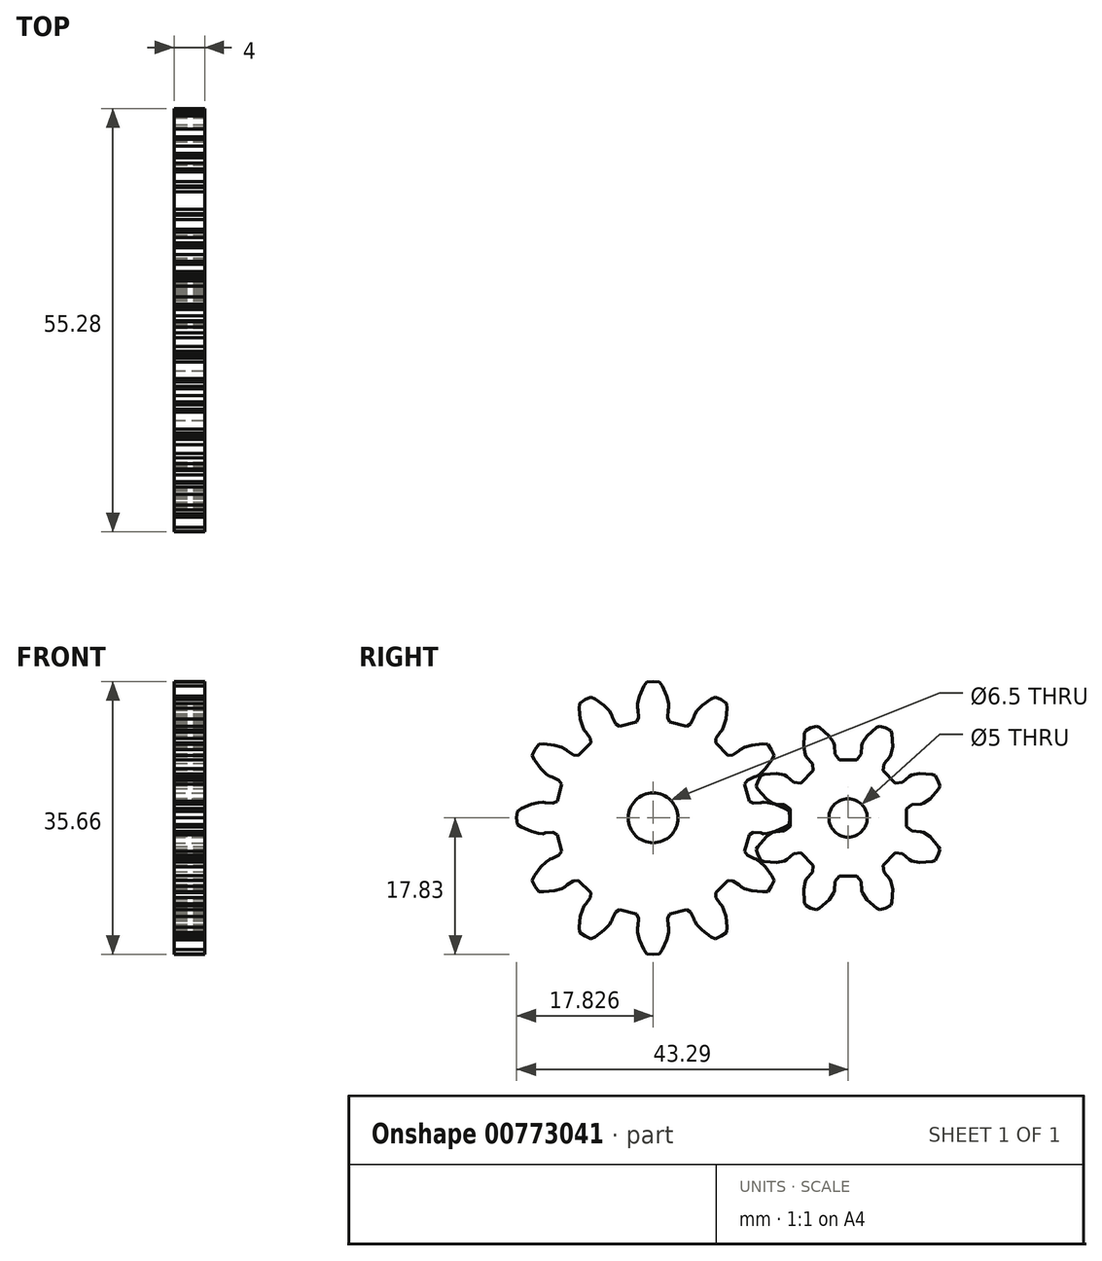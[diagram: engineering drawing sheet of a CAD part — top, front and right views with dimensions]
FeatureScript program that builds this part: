
annotation { "Feature Type Name" : "Feature", "Feature Type Description" : "" }
export const myFeature = defineFeature(function(context is Context, id is Id, definition is map)
    precondition{}
    {
        {
            var Q0;
            Q0=qCreatedBy(makeId("Right.planeOp"),FACE);
            var sketch = newSketch(context, id + "F0", { "sketchPlane" : qUnion([Q0])});
            skLineSegment(sketch, "E0", {"start": v(5.14, -9.6) * mm, "end": v(5.62, -8.91) * mm});
            skLineSegment(sketch, "E1", {"start": v(5.62, -8.91) * mm, "end": v(5.98, -8.15) * mm});
            skLineSegment(sketch, "E2", {"start": v(5.98, -8.15) * mm, "end": v(5.69, -7.55) * mm});
            skLineSegment(sketch, "E3", {"start": v(5.69, -7.55) * mm, "end": v(4.86, -6.4) * mm});
            skLineSegment(sketch, "E4", {"start": v(4.86, -6.4) * mm, "end": v(4.16, -5.74) * mm});
            skLineSegment(sketch, "E5", {"start": v(4.16, -5.74) * mm, "end": v(3.72, -5.44) * mm});
            skLineSegment(sketch, "E6", {"start": v(3.72, -5.44) * mm, "end": v(3.64, -5.4) * mm});
            skLineSegment(sketch, "E7", {"start": v(3.64, -5.4) * mm, "end": v(3.38, -5.34) * mm});
            skLineSegment(sketch, "E8", {"start": v(3.38, -5.34) * mm, "end": v(2.49, -4.9) * mm});
            skLineSegment(sketch, "E9", {"start": v(2.49, -4.9) * mm, "end": v(2.14, -4.38) * mm});
            skLineSegment(sketch, "E10", {"start": v(2.14, -4.38) * mm, "end": v(2.73, -2.18) * mm});
            skLineSegment(sketch, "E11", {"start": v(2.73, -2.18) * mm, "end": v(3.29, -1.91) * mm});
            skLineSegment(sketch, "E12", {"start": v(3.29, -1.91) * mm, "end": v(4.29, -1.97) * mm});
            skLineSegment(sketch, "E13", {"start": v(4.29, -1.97) * mm, "end": v(4.54, -2.04) * mm});
            skLineSegment(sketch, "E14", {"start": v(4.54, -2.04) * mm, "end": v(4.62, -2.05) * mm});
            skLineSegment(sketch, "E15", {"start": v(4.62, -2.05) * mm, "end": v(5.15, -2.02) * mm});
            skLineSegment(sketch, "E16", {"start": v(5.15, -2.02) * mm, "end": v(6.1, -1.79) * mm});
            skLineSegment(sketch, "E17", {"start": v(6.1, -1.79) * mm, "end": v(7.39, -1.21) * mm});
            skLineSegment(sketch, "E18", {"start": v(7.39, -1.21) * mm, "end": v(7.94, -0.84) * mm});
            skLineSegment(sketch, "E19", {"start": v(7.94, -0.84) * mm, "end": v(8.01, 0) * mm});
            skLineSegment(sketch, "E20", {"start": v(8.01, 0) * mm, "end": v(7.94, 0.84) * mm});
            skLineSegment(sketch, "E21", {"start": v(7.94, 0.84) * mm, "end": v(7.39, 1.21) * mm});
            skLineSegment(sketch, "E22", {"start": v(7.39, 1.21) * mm, "end": v(6.1, 1.79) * mm});
            skLineSegment(sketch, "E23", {"start": v(6.1, 1.79) * mm, "end": v(5.15, 2.02) * mm});
            skLineSegment(sketch, "E24", {"start": v(5.15, 2.02) * mm, "end": v(4.62, 2.05) * mm});
            skLineSegment(sketch, "E25", {"start": v(4.62, 2.05) * mm, "end": v(4.54, 2.04) * mm});
            skLineSegment(sketch, "E26", {"start": v(4.54, 2.04) * mm, "end": v(4.29, 1.97) * mm});
            skLineSegment(sketch, "E27", {"start": v(4.29, 1.97) * mm, "end": v(3.29, 1.91) * mm});
            skLineSegment(sketch, "E28", {"start": v(3.29, 1.91) * mm, "end": v(2.73, 2.18) * mm});
            skLineSegment(sketch, "E29", {"start": v(2.73, 2.18) * mm, "end": v(2.14, 4.38) * mm});
            skLineSegment(sketch, "E30", {"start": v(2.14, 4.38) * mm, "end": v(2.49, 4.9) * mm});
            skLineSegment(sketch, "E31", {"start": v(2.49, 4.9) * mm, "end": v(3.38, 5.34) * mm});
            skLineSegment(sketch, "E32", {"start": v(3.38, 5.34) * mm, "end": v(3.64, 5.4) * mm});
            skLineSegment(sketch, "E33", {"start": v(3.64, 5.4) * mm, "end": v(3.72, 5.44) * mm});
            skLineSegment(sketch, "E34", {"start": v(3.72, 5.44) * mm, "end": v(4.16, 5.74) * mm});
            skLineSegment(sketch, "E35", {"start": v(4.16, 5.74) * mm, "end": v(4.86, 6.4) * mm});
            skLineSegment(sketch, "E36", {"start": v(4.86, 6.4) * mm, "end": v(5.69, 7.55) * mm});
            skLineSegment(sketch, "E37", {"start": v(5.69, 7.55) * mm, "end": v(5.98, 8.15) * mm});
            skLineSegment(sketch, "E38", {"start": v(5.98, 8.15) * mm, "end": v(5.62, 8.91) * mm});
            skLineSegment(sketch, "E39", {"start": v(5.62, 8.91) * mm, "end": v(5.14, 9.6) * mm});
            skLineSegment(sketch, "E40", {"start": v(5.14, 9.6) * mm, "end": v(4.48, 9.65) * mm});
            skLineSegment(sketch, "E41", {"start": v(4.48, 9.65) * mm, "end": v(3.07, 9.5) * mm});
            skLineSegment(sketch, "E42", {"start": v(3.07, 9.5) * mm, "end": v(2.14, 9.23) * mm});
            skLineSegment(sketch, "E43", {"start": v(2.14, 9.23) * mm, "end": v(1.66, 9) * mm});
            skLineSegment(sketch, "E44", {"start": v(1.66, 9) * mm, "end": v(1.6, 8.95) * mm});
            skLineSegment(sketch, "E45", {"start": v(1.6, 8.95) * mm, "end": v(1.41, 8.76) * mm});
            skLineSegment(sketch, "E46", {"start": v(1.41, 8.76) * mm, "end": v(0.58, 8.2) * mm});
            skLineSegment(sketch, "E47", {"start": v(0.58, 8.2) * mm, "end": v(-0.04, 8.16) * mm});
            skLineSegment(sketch, "E48", {"start": v(-0.04, 8.16) * mm, "end": v(-1.65, 9.77) * mm});
            skLineSegment(sketch, "E49", {"start": v(-1.65, 9.77) * mm, "end": v(-1.6, 10.4) * mm});
            skLineSegment(sketch, "E50", {"start": v(-1.6, 10.4) * mm, "end": v(-1.06, 11.23) * mm});
            skLineSegment(sketch, "E51", {"start": v(-1.06, 11.23) * mm, "end": v(-0.87, 11.4) * mm});
            skLineSegment(sketch, "E52", {"start": v(-0.87, 11.4) * mm, "end": v(-0.82, 11.48) * mm});
            skLineSegment(sketch, "E53", {"start": v(-0.82, 11.48) * mm, "end": v(-0.58, 11.95) * mm});
            skLineSegment(sketch, "E54", {"start": v(-0.58, 11.95) * mm, "end": v(-0.31, 12.88) * mm});
            skLineSegment(sketch, "E55", {"start": v(-0.31, 12.88) * mm, "end": v(-0.16, 14.29) * mm});
            skLineSegment(sketch, "E56", {"start": v(-0.16, 14.29) * mm, "end": v(-0.2, 14.95) * mm});
            skLineSegment(sketch, "E57", {"start": v(-0.2, 14.95) * mm, "end": v(-0.9, 15.44) * mm});
            skLineSegment(sketch, "E58", {"start": v(-0.9, 15.44) * mm, "end": v(-1.67, 15.8) * mm});
            skLineSegment(sketch, "E59", {"start": v(-1.67, 15.8) * mm, "end": v(-2.26, 15.5) * mm});
            skLineSegment(sketch, "E60", {"start": v(-2.26, 15.5) * mm, "end": v(-3.4, 14.67) * mm});
            skLineSegment(sketch, "E61", {"start": v(-3.4, 14.67) * mm, "end": v(-4.08, 13.97) * mm});
            skLineSegment(sketch, "E62", {"start": v(-4.08, 13.97) * mm, "end": v(-4.37, 13.53) * mm});
            skLineSegment(sketch, "E63", {"start": v(-4.37, 13.53) * mm, "end": v(-4.41, 13.45) * mm});
            skLineSegment(sketch, "E64", {"start": v(-4.41, 13.45) * mm, "end": v(-4.47, 13.2) * mm});
            skLineSegment(sketch, "E65", {"start": v(-4.47, 13.2) * mm, "end": v(-4.92, 12.3) * mm});
            skLineSegment(sketch, "E66", {"start": v(-4.92, 12.3) * mm, "end": v(-5.43, 11.96) * mm});
            skLineSegment(sketch, "E67", {"start": v(-5.43, 11.96) * mm, "end": v(-7.63, 12.54) * mm});
            skLineSegment(sketch, "E68", {"start": v(-7.63, 12.54) * mm, "end": v(-7.9, 13.1) * mm});
            skLineSegment(sketch, "E69", {"start": v(-7.9, 13.1) * mm, "end": v(-7.84, 14.1) * mm});
            skLineSegment(sketch, "E70", {"start": v(-7.84, 14.1) * mm, "end": v(-7.77, 14.35) * mm});
            skLineSegment(sketch, "E71", {"start": v(-7.77, 14.35) * mm, "end": v(-7.76, 14.44) * mm});
            skLineSegment(sketch, "E72", {"start": v(-7.76, 14.44) * mm, "end": v(-7.8, 14.97) * mm});
            skLineSegment(sketch, "E73", {"start": v(-7.8, 14.97) * mm, "end": v(-8.03, 15.9) * mm});
            skLineSegment(sketch, "E74", {"start": v(-8.03, 15.9) * mm, "end": v(-8.6, 17.2) * mm});
            skLineSegment(sketch, "E75", {"start": v(-8.6, 17.2) * mm, "end": v(-8.97, 17.75) * mm});
            skLineSegment(sketch, "E76", {"start": v(-8.97, 17.75) * mm, "end": v(-9.81, 17.83) * mm});
            skLineSegment(sketch, "E77", {"start": v(-9.81, 17.83) * mm, "end": v(-10.66, 17.75) * mm});
            skLineSegment(sketch, "E78", {"start": v(-10.66, 17.75) * mm, "end": v(-11.03, 17.2) * mm});
            skLineSegment(sketch, "E79", {"start": v(-11.03, 17.2) * mm, "end": v(-11.6, 15.9) * mm});
            skLineSegment(sketch, "E80", {"start": v(-11.6, 15.9) * mm, "end": v(-11.83, 14.97) * mm});
            skLineSegment(sketch, "E81", {"start": v(-11.83, 14.97) * mm, "end": v(-11.87, 14.44) * mm});
            skLineSegment(sketch, "E82", {"start": v(-11.87, 14.44) * mm, "end": v(-11.86, 14.35) * mm});
            skLineSegment(sketch, "E83", {"start": v(-11.86, 14.35) * mm, "end": v(-11.79, 14.1) * mm});
            skLineSegment(sketch, "E84", {"start": v(-11.79, 14.1) * mm, "end": v(-11.73, 13.1) * mm});
            skLineSegment(sketch, "E85", {"start": v(-11.73, 13.1) * mm, "end": v(-12, 12.54) * mm});
            skLineSegment(sketch, "E86", {"start": v(-12, 12.54) * mm, "end": v(-14.2, 11.96) * mm});
            skLineSegment(sketch, "E87", {"start": v(-14.2, 11.96) * mm, "end": v(-14.71, 12.3) * mm});
            skLineSegment(sketch, "E88", {"start": v(-14.71, 12.3) * mm, "end": v(-15.16, 13.2) * mm});
            skLineSegment(sketch, "E89", {"start": v(-15.16, 13.2) * mm, "end": v(-15.22, 13.45) * mm});
            skLineSegment(sketch, "E90", {"start": v(-15.22, 13.45) * mm, "end": v(-15.25, 13.53) * mm});
            skLineSegment(sketch, "E91", {"start": v(-15.25, 13.53) * mm, "end": v(-15.55, 13.97) * mm});
            skLineSegment(sketch, "E92", {"start": v(-15.55, 13.97) * mm, "end": v(-16.22, 14.67) * mm});
            skLineSegment(sketch, "E93", {"start": v(-16.22, 14.67) * mm, "end": v(-17.36, 15.5) * mm});
            skLineSegment(sketch, "E94", {"start": v(-17.36, 15.5) * mm, "end": v(-17.96, 15.8) * mm});
            skLineSegment(sketch, "E95", {"start": v(-17.96, 15.8) * mm, "end": v(-18.73, 15.44) * mm});
            skLineSegment(sketch, "E96", {"start": v(-18.73, 15.44) * mm, "end": v(-19.42, 14.95) * mm});
            skLineSegment(sketch, "E97", {"start": v(-19.42, 14.95) * mm, "end": v(-19.47, 14.29) * mm});
            skLineSegment(sketch, "E98", {"start": v(-19.47, 14.29) * mm, "end": v(-19.32, 12.88) * mm});
            skLineSegment(sketch, "E99", {"start": v(-19.32, 12.88) * mm, "end": v(-19.05, 11.95) * mm});
            skLineSegment(sketch, "E100", {"start": v(-19.05, 11.95) * mm, "end": v(-18.81, 11.48) * mm});
            skLineSegment(sketch, "E101", {"start": v(-18.81, 11.48) * mm, "end": v(-18.76, 11.4) * mm});
            skLineSegment(sketch, "E102", {"start": v(-18.76, 11.4) * mm, "end": v(-18.57, 11.23) * mm});
            skLineSegment(sketch, "E103", {"start": v(-18.57, 11.23) * mm, "end": v(-18.02, 10.4) * mm});
            skLineSegment(sketch, "E104", {"start": v(-18.02, 10.4) * mm, "end": v(-17.98, 9.77) * mm});
            skLineSegment(sketch, "E105", {"start": v(-17.98, 9.77) * mm, "end": v(-19.59, 8.16) * mm});
            skLineSegment(sketch, "E106", {"start": v(-19.59, 8.16) * mm, "end": v(-20.2, 8.2) * mm});
            skLineSegment(sketch, "E107", {"start": v(-20.2, 8.2) * mm, "end": v(-21.04, 8.76) * mm});
            skLineSegment(sketch, "E108", {"start": v(-21.04, 8.76) * mm, "end": v(-21.22, 8.95) * mm});
            skLineSegment(sketch, "E109", {"start": v(-21.22, 8.95) * mm, "end": v(-21.3, 9) * mm});
            skLineSegment(sketch, "E110", {"start": v(-21.3, 9) * mm, "end": v(-21.77, 9.23) * mm});
            skLineSegment(sketch, "E111", {"start": v(-21.77, 9.23) * mm, "end": v(-22.7, 9.5) * mm});
            skLineSegment(sketch, "E112", {"start": v(-22.7, 9.5) * mm, "end": v(-24.1, 9.65) * mm});
            skLineSegment(sketch, "E113", {"start": v(-24.1, 9.65) * mm, "end": v(-24.77, 9.6) * mm});
            skLineSegment(sketch, "E114", {"start": v(-24.77, 9.6) * mm, "end": v(-25.25, 8.91) * mm});
            skLineSegment(sketch, "E115", {"start": v(-25.25, 8.91) * mm, "end": v(-25.6, 8.15) * mm});
            skLineSegment(sketch, "E116", {"start": v(-25.6, 8.15) * mm, "end": v(-25.32, 7.55) * mm});
            skLineSegment(sketch, "E117", {"start": v(-25.32, 7.55) * mm, "end": v(-24.48, 6.4) * mm});
            skLineSegment(sketch, "E118", {"start": v(-24.48, 6.4) * mm, "end": v(-23.78, 5.74) * mm});
            skLineSegment(sketch, "E119", {"start": v(-23.78, 5.74) * mm, "end": v(-23.34, 5.44) * mm});
            skLineSegment(sketch, "E120", {"start": v(-23.34, 5.44) * mm, "end": v(-23.26, 5.4) * mm});
            skLineSegment(sketch, "E121", {"start": v(-23.26, 5.4) * mm, "end": v(-23.01, 5.34) * mm});
            skLineSegment(sketch, "E122", {"start": v(-23.01, 5.34) * mm, "end": v(-22.12, 4.9) * mm});
            skLineSegment(sketch, "E123", {"start": v(-22.12, 4.9) * mm, "end": v(-21.77, 4.38) * mm});
            skLineSegment(sketch, "E124", {"start": v(-21.77, 4.38) * mm, "end": v(-22.36, 2.18) * mm});
            skLineSegment(sketch, "E125", {"start": v(-22.36, 2.18) * mm, "end": v(-22.92, 1.91) * mm});
            skLineSegment(sketch, "E126", {"start": v(-22.92, 1.91) * mm, "end": v(-23.92, 1.97) * mm});
            skLineSegment(sketch, "E127", {"start": v(-23.92, 1.97) * mm, "end": v(-24.16, 2.04) * mm});
            skLineSegment(sketch, "E128", {"start": v(-24.16, 2.04) * mm, "end": v(-24.25, 2.05) * mm});
            skLineSegment(sketch, "E129", {"start": v(-24.25, 2.05) * mm, "end": v(-24.78, 2.02) * mm});
            skLineSegment(sketch, "E130", {"start": v(-24.78, 2.02) * mm, "end": v(-25.72, 1.79) * mm});
            skLineSegment(sketch, "E131", {"start": v(-25.72, 1.79) * mm, "end": v(-27.02, 1.21) * mm});
            skLineSegment(sketch, "E132", {"start": v(-27.02, 1.21) * mm, "end": v(-27.57, 0.84) * mm});
            skLineSegment(sketch, "E133", {"start": v(-27.57, 0.84) * mm, "end": v(-27.64, 0) * mm});
            skLineSegment(sketch, "E134", {"start": v(-27.64, 0) * mm, "end": v(-27.57, -0.84) * mm});
            skLineSegment(sketch, "E135", {"start": v(-27.57, -0.84) * mm, "end": v(-27.02, -1.21) * mm});
            skLineSegment(sketch, "E136", {"start": v(-27.02, -1.21) * mm, "end": v(-25.72, -1.79) * mm});
            skLineSegment(sketch, "E137", {"start": v(-25.72, -1.79) * mm, "end": v(-24.78, -2.02) * mm});
            skLineSegment(sketch, "E138", {"start": v(-24.78, -2.02) * mm, "end": v(-24.25, -2.05) * mm});
            skLineSegment(sketch, "E139", {"start": v(-24.25, -2.05) * mm, "end": v(-24.16, -2.04) * mm});
            skLineSegment(sketch, "E140", {"start": v(-24.16, -2.04) * mm, "end": v(-23.92, -1.97) * mm});
            skLineSegment(sketch, "E141", {"start": v(-23.92, -1.97) * mm, "end": v(-22.92, -1.91) * mm});
            skLineSegment(sketch, "E142", {"start": v(-22.92, -1.91) * mm, "end": v(-22.36, -2.18) * mm});
            skLineSegment(sketch, "E143", {"start": v(-22.36, -2.18) * mm, "end": v(-21.77, -4.38) * mm});
            skLineSegment(sketch, "E144", {"start": v(-21.77, -4.38) * mm, "end": v(-22.12, -4.9) * mm});
            skLineSegment(sketch, "E145", {"start": v(-22.12, -4.9) * mm, "end": v(-23.01, -5.34) * mm});
            skLineSegment(sketch, "E146", {"start": v(-23.01, -5.34) * mm, "end": v(-23.26, -5.4) * mm});
            skLineSegment(sketch, "E147", {"start": v(-23.26, -5.4) * mm, "end": v(-23.34, -5.44) * mm});
            skLineSegment(sketch, "E148", {"start": v(-23.34, -5.44) * mm, "end": v(-23.78, -5.74) * mm});
            skLineSegment(sketch, "E149", {"start": v(-23.78, -5.74) * mm, "end": v(-24.48, -6.4) * mm});
            skLineSegment(sketch, "E150", {"start": v(-24.48, -6.4) * mm, "end": v(-25.32, -7.55) * mm});
            skLineSegment(sketch, "E151", {"start": v(-25.32, -7.55) * mm, "end": v(-25.6, -8.15) * mm});
            skLineSegment(sketch, "E152", {"start": v(-25.6, -8.15) * mm, "end": v(-25.25, -8.91) * mm});
            skLineSegment(sketch, "E153", {"start": v(-25.25, -8.91) * mm, "end": v(-24.77, -9.6) * mm});
            skLineSegment(sketch, "E154", {"start": v(-24.77, -9.6) * mm, "end": v(-24.1, -9.65) * mm});
            skLineSegment(sketch, "E155", {"start": v(-24.1, -9.65) * mm, "end": v(-22.7, -9.5) * mm});
            skLineSegment(sketch, "E156", {"start": v(-22.7, -9.5) * mm, "end": v(-21.77, -9.23) * mm});
            skLineSegment(sketch, "E157", {"start": v(-21.77, -9.23) * mm, "end": v(-21.3, -9) * mm});
            skLineSegment(sketch, "E158", {"start": v(-21.3, -9) * mm, "end": v(-21.22, -8.95) * mm});
            skLineSegment(sketch, "E159", {"start": v(-21.22, -8.95) * mm, "end": v(-21.04, -8.76) * mm});
            skLineSegment(sketch, "E160", {"start": v(-21.04, -8.76) * mm, "end": v(-20.2, -8.2) * mm});
            skLineSegment(sketch, "E161", {"start": v(-20.2, -8.2) * mm, "end": v(-19.59, -8.16) * mm});
            skLineSegment(sketch, "E162", {"start": v(-19.59, -8.16) * mm, "end": v(-17.98, -9.77) * mm});
            skLineSegment(sketch, "E163", {"start": v(-17.98, -9.77) * mm, "end": v(-18.02, -10.4) * mm});
            skLineSegment(sketch, "E164", {"start": v(-18.02, -10.4) * mm, "end": v(-18.57, -11.23) * mm});
            skLineSegment(sketch, "E165", {"start": v(-18.57, -11.23) * mm, "end": v(-18.76, -11.4) * mm});
            skLineSegment(sketch, "E166", {"start": v(-18.76, -11.4) * mm, "end": v(-18.81, -11.48) * mm});
            skLineSegment(sketch, "E167", {"start": v(-18.81, -11.48) * mm, "end": v(-19.05, -11.95) * mm});
            skLineSegment(sketch, "E168", {"start": v(-19.05, -11.95) * mm, "end": v(-19.32, -12.88) * mm});
            skLineSegment(sketch, "E169", {"start": v(-19.32, -12.88) * mm, "end": v(-19.47, -14.29) * mm});
            skLineSegment(sketch, "E170", {"start": v(-19.47, -14.29) * mm, "end": v(-19.42, -14.95) * mm});
            skLineSegment(sketch, "E171", {"start": v(-19.42, -14.95) * mm, "end": v(-18.73, -15.44) * mm});
            skLineSegment(sketch, "E172", {"start": v(-18.73, -15.44) * mm, "end": v(-17.96, -15.8) * mm});
            skLineSegment(sketch, "E173", {"start": v(-17.96, -15.8) * mm, "end": v(-17.36, -15.5) * mm});
            skLineSegment(sketch, "E174", {"start": v(-17.36, -15.5) * mm, "end": v(-16.22, -14.67) * mm});
            skLineSegment(sketch, "E175", {"start": v(-16.22, -14.67) * mm, "end": v(-15.55, -13.97) * mm});
            skLineSegment(sketch, "E176", {"start": v(-15.55, -13.97) * mm, "end": v(-15.25, -13.53) * mm});
            skLineSegment(sketch, "E177", {"start": v(-15.25, -13.53) * mm, "end": v(-15.22, -13.45) * mm});
            skLineSegment(sketch, "E178", {"start": v(-15.22, -13.45) * mm, "end": v(-15.16, -13.2) * mm});
            skLineSegment(sketch, "E179", {"start": v(-15.16, -13.2) * mm, "end": v(-14.71, -12.3) * mm});
            skLineSegment(sketch, "E180", {"start": v(-14.71, -12.3) * mm, "end": v(-14.2, -11.96) * mm});
            skLineSegment(sketch, "E181", {"start": v(-14.2, -11.96) * mm, "end": v(-12, -12.54) * mm});
            skLineSegment(sketch, "E182", {"start": v(-12, -12.54) * mm, "end": v(-11.73, -13.1) * mm});
            skLineSegment(sketch, "E183", {"start": v(-11.73, -13.1) * mm, "end": v(-11.79, -14.1) * mm});
            skLineSegment(sketch, "E184", {"start": v(-11.79, -14.1) * mm, "end": v(-11.86, -14.35) * mm});
            skLineSegment(sketch, "E185", {"start": v(-11.86, -14.35) * mm, "end": v(-11.87, -14.44) * mm});
            skLineSegment(sketch, "E186", {"start": v(-11.87, -14.44) * mm, "end": v(-11.83, -14.97) * mm});
            skLineSegment(sketch, "E187", {"start": v(-11.83, -14.97) * mm, "end": v(-11.6, -15.9) * mm});
            skLineSegment(sketch, "E188", {"start": v(-11.6, -15.9) * mm, "end": v(-11.03, -17.2) * mm});
            skLineSegment(sketch, "E189", {"start": v(-11.03, -17.2) * mm, "end": v(-10.66, -17.75) * mm});
            skLineSegment(sketch, "E190", {"start": v(-10.66, -17.75) * mm, "end": v(-9.81, -17.83) * mm});
            skLineSegment(sketch, "E191", {"start": v(-9.81, -17.83) * mm, "end": v(-8.97, -17.75) * mm});
            skLineSegment(sketch, "E192", {"start": v(-8.97, -17.75) * mm, "end": v(-8.6, -17.2) * mm});
            skLineSegment(sketch, "E193", {"start": v(-8.6, -17.2) * mm, "end": v(-8.03, -15.9) * mm});
            skLineSegment(sketch, "E194", {"start": v(-8.03, -15.9) * mm, "end": v(-7.8, -14.97) * mm});
            skLineSegment(sketch, "E195", {"start": v(-7.8, -14.97) * mm, "end": v(-7.76, -14.44) * mm});
            skLineSegment(sketch, "E196", {"start": v(-7.76, -14.44) * mm, "end": v(-7.77, -14.35) * mm});
            skLineSegment(sketch, "E197", {"start": v(-7.77, -14.35) * mm, "end": v(-7.84, -14.1) * mm});
            skLineSegment(sketch, "E198", {"start": v(-7.84, -14.1) * mm, "end": v(-7.9, -13.1) * mm});
            skLineSegment(sketch, "E199", {"start": v(-7.9, -13.1) * mm, "end": v(-7.63, -12.54) * mm});
            skLineSegment(sketch, "E200", {"start": v(-7.63, -12.54) * mm, "end": v(-5.43, -11.96) * mm});
            skLineSegment(sketch, "E201", {"start": v(-5.43, -11.96) * mm, "end": v(-4.92, -12.3) * mm});
            skLineSegment(sketch, "E202", {"start": v(-4.92, -12.3) * mm, "end": v(-4.47, -13.2) * mm});
            skLineSegment(sketch, "E203", {"start": v(-4.47, -13.2) * mm, "end": v(-4.41, -13.45) * mm});
            skLineSegment(sketch, "E204", {"start": v(-4.41, -13.45) * mm, "end": v(-4.37, -13.53) * mm});
            skLineSegment(sketch, "E205", {"start": v(-4.37, -13.53) * mm, "end": v(-4.08, -13.97) * mm});
            skLineSegment(sketch, "E206", {"start": v(-4.08, -13.97) * mm, "end": v(-3.4, -14.67) * mm});
            skLineSegment(sketch, "E207", {"start": v(-3.4, -14.67) * mm, "end": v(-2.26, -15.5) * mm});
            skLineSegment(sketch, "E208", {"start": v(-2.26, -15.5) * mm, "end": v(-1.67, -15.8) * mm});
            skLineSegment(sketch, "E209", {"start": v(-1.67, -15.8) * mm, "end": v(-0.9, -15.44) * mm});
            skLineSegment(sketch, "E210", {"start": v(-0.9, -15.44) * mm, "end": v(-0.2, -14.95) * mm});
            skLineSegment(sketch, "E211", {"start": v(-0.2, -14.95) * mm, "end": v(-0.16, -14.29) * mm});
            skLineSegment(sketch, "E212", {"start": v(-0.16, -14.29) * mm, "end": v(-0.31, -12.88) * mm});
            skLineSegment(sketch, "E213", {"start": v(-0.31, -12.88) * mm, "end": v(-0.58, -11.95) * mm});
            skLineSegment(sketch, "E214", {"start": v(-0.58, -11.95) * mm, "end": v(-0.82, -11.48) * mm});
            skLineSegment(sketch, "E215", {"start": v(-0.82, -11.48) * mm, "end": v(-0.87, -11.4) * mm});
            skLineSegment(sketch, "E216", {"start": v(-0.87, -11.4) * mm, "end": v(-1.06, -11.23) * mm});
            skLineSegment(sketch, "E217", {"start": v(-1.06, -11.23) * mm, "end": v(-1.6, -10.4) * mm});
            skLineSegment(sketch, "E218", {"start": v(-1.6, -10.4) * mm, "end": v(-1.65, -9.77) * mm});
            skLineSegment(sketch, "E219", {"start": v(-1.65, -9.77) * mm, "end": v(-0.04, -8.16) * mm});
            skLineSegment(sketch, "E220", {"start": v(-0.04, -8.16) * mm, "end": v(0.58, -8.2) * mm});
            skLineSegment(sketch, "E221", {"start": v(0.58, -8.2) * mm, "end": v(1.41, -8.76) * mm});
            skLineSegment(sketch, "E222", {"start": v(1.41, -8.76) * mm, "end": v(1.6, -8.95) * mm});
            skLineSegment(sketch, "E223", {"start": v(1.6, -8.95) * mm, "end": v(1.66, -9) * mm});
            skLineSegment(sketch, "E224", {"start": v(1.66, -9) * mm, "end": v(2.14, -9.23) * mm});
            skLineSegment(sketch, "E225", {"start": v(2.14, -9.23) * mm, "end": v(3.07, -9.5) * mm});
            skLineSegment(sketch, "E226", {"start": v(3.07, -9.5) * mm, "end": v(4.48, -9.65) * mm});
            skLineSegment(sketch, "E227", {"start": v(4.48, -9.65) * mm, "end": v(5.14, -9.6) * mm});
            skLineSegment(sketch, "E228", {"start": v(-9.4, -1.96) * mm, "end": v(-9.81, -2) * mm});
            skLineSegment(sketch, "E229", {"start": v(-9.81, -2) * mm, "end": v(-10.23, -1.96) * mm});
            skLineSegment(sketch, "E230", {"start": v(-10.23, -1.96) * mm, "end": v(-10.63, -1.83) * mm});
            skLineSegment(sketch, "E231", {"start": v(-10.63, -1.83) * mm, "end": v(-10.99, -1.62) * mm});
            skLineSegment(sketch, "E232", {"start": v(-10.99, -1.62) * mm, "end": v(-11.3, -1.34) * mm});
            skLineSegment(sketch, "E233", {"start": v(-11.3, -1.34) * mm, "end": v(-11.55, -1) * mm});
            skLineSegment(sketch, "E234", {"start": v(-11.55, -1) * mm, "end": v(-11.72, -0.62) * mm});
            skLineSegment(sketch, "E235", {"start": v(-11.72, -0.62) * mm, "end": v(-11.8, -0.2) * mm});
            skLineSegment(sketch, "E236", {"start": v(-11.8, -0.2) * mm, "end": v(-11.8, 0.2) * mm});
            skLineSegment(sketch, "E237", {"start": v(-11.8, 0.2) * mm, "end": v(-11.72, 0.62) * mm});
            skLineSegment(sketch, "E238", {"start": v(-11.72, 0.62) * mm, "end": v(-11.55, 1) * mm});
            skLineSegment(sketch, "E239", {"start": v(-11.55, 1) * mm, "end": v(-11.3, 1.34) * mm});
            skLineSegment(sketch, "E240", {"start": v(-11.3, 1.34) * mm, "end": v(-10.99, 1.62) * mm});
            skLineSegment(sketch, "E241", {"start": v(-10.99, 1.62) * mm, "end": v(-10.63, 1.83) * mm});
            skLineSegment(sketch, "E242", {"start": v(-10.63, 1.83) * mm, "end": v(-10.23, 1.96) * mm});
            skLineSegment(sketch, "E243", {"start": v(-10.23, 1.96) * mm, "end": v(-9.81, 2) * mm});
            skLineSegment(sketch, "E244", {"start": v(-9.81, 2) * mm, "end": v(-9.4, 1.96) * mm});
            skLineSegment(sketch, "E245", {"start": v(-9.4, 1.96) * mm, "end": v(-9, 1.83) * mm});
            skLineSegment(sketch, "E246", {"start": v(-9, 1.83) * mm, "end": v(-8.64, 1.62) * mm});
            skLineSegment(sketch, "E247", {"start": v(-8.64, 1.62) * mm, "end": v(-8.33, 1.34) * mm});
            skLineSegment(sketch, "E248", {"start": v(-8.33, 1.34) * mm, "end": v(-8.08, 1) * mm});
            skLineSegment(sketch, "E249", {"start": v(-8.08, 1) * mm, "end": v(-7.91, 0.62) * mm});
            skLineSegment(sketch, "E250", {"start": v(-7.91, 0.62) * mm, "end": v(-7.83, 0.2) * mm});
            skLineSegment(sketch, "E251", {"start": v(-7.83, 0.2) * mm, "end": v(-7.83, -0.2) * mm});
            skLineSegment(sketch, "E252", {"start": v(-7.83, -0.2) * mm, "end": v(-7.91, -0.62) * mm});
            skLineSegment(sketch, "E253", {"start": v(-7.91, -0.62) * mm, "end": v(-8.08, -1) * mm});
            skLineSegment(sketch, "E254", {"start": v(-8.08, -1) * mm, "end": v(-8.33, -1.34) * mm});
            skLineSegment(sketch, "E255", {"start": v(-8.33, -1.34) * mm, "end": v(-8.64, -1.62) * mm});
            skLineSegment(sketch, "E256", {"start": v(-8.64, -1.62) * mm, "end": v(-9, -1.83) * mm});
            skLineSegment(sketch, "E257", {"start": v(-9, -1.83) * mm, "end": v(-9.4, -1.96) * mm});
            skLineSegment(sketch, "E258", {"start": v(4.25, 5.56) * mm, "end": v(3.89, 4.87) * mm});
            skLineSegment(sketch, "E259", {"start": v(3.89, 4.87) * mm, "end": v(3.66, 4.13) * mm});
            skLineSegment(sketch, "E260", {"start": v(3.66, 4.13) * mm, "end": v(3.84, 3.76) * mm});
            skLineSegment(sketch, "E261", {"start": v(3.84, 3.76) * mm, "end": v(4.96, 2.48) * mm});
            skLineSegment(sketch, "E262", {"start": v(4.96, 2.48) * mm, "end": v(5.8, 1.9) * mm});
            skLineSegment(sketch, "E263", {"start": v(5.8, 1.9) * mm, "end": v(6.15, 1.8) * mm});
            skLineSegment(sketch, "E264", {"start": v(6.15, 1.8) * mm, "end": v(7.33, 1.71) * mm});
            skLineSegment(sketch, "E265", {"start": v(7.33, 1.71) * mm, "end": v(8.06, 1.14) * mm});
            skLineSegment(sketch, "E266", {"start": v(8.06, 1.14) * mm, "end": v(8.06, -1.14) * mm});
            skLineSegment(sketch, "E267", {"start": v(8.06, -1.14) * mm, "end": v(7.33, -1.71) * mm});
            skLineSegment(sketch, "E268", {"start": v(7.33, -1.71) * mm, "end": v(6.15, -1.8) * mm});
            skLineSegment(sketch, "E269", {"start": v(6.15, -1.8) * mm, "end": v(5.8, -1.9) * mm});
            skLineSegment(sketch, "E270", {"start": v(5.8, -1.9) * mm, "end": v(4.96, -2.48) * mm});
            skLineSegment(sketch, "E271", {"start": v(4.96, -2.48) * mm, "end": v(3.84, -3.76) * mm});
            skLineSegment(sketch, "E272", {"start": v(3.84, -3.76) * mm, "end": v(3.66, -4.13) * mm});
            skLineSegment(sketch, "E273", {"start": v(3.66, -4.13) * mm, "end": v(3.89, -4.87) * mm});
            skLineSegment(sketch, "E274", {"start": v(3.89, -4.87) * mm, "end": v(4.25, -5.56) * mm});
            skLineSegment(sketch, "E275", {"start": v(4.25, -5.56) * mm, "end": v(4.65, -5.7) * mm});
            skLineSegment(sketch, "E276", {"start": v(4.65, -5.7) * mm, "end": v(6.33, -5.8) * mm});
            skLineSegment(sketch, "E277", {"start": v(6.33, -5.8) * mm, "end": v(7.34, -5.6) * mm});
            skLineSegment(sketch, "E278", {"start": v(7.34, -5.6) * mm, "end": v(7.67, -5.45) * mm});
            skLineSegment(sketch, "E279", {"start": v(7.67, -5.45) * mm, "end": v(8.56, -4.67) * mm});
            skLineSegment(sketch, "E280", {"start": v(8.56, -4.67) * mm, "end": v(9.48, -4.56) * mm});
            skLineSegment(sketch, "E281", {"start": v(9.48, -4.56) * mm, "end": v(11.09, -6.17) * mm});
            skLineSegment(sketch, "E282", {"start": v(11.09, -6.17) * mm, "end": v(10.98, -7.1) * mm});
            skLineSegment(sketch, "E283", {"start": v(10.98, -7.1) * mm, "end": v(10.2, -7.98) * mm});
            skLineSegment(sketch, "E284", {"start": v(10.2, -7.98) * mm, "end": v(10.04, -8.3) * mm});
            skLineSegment(sketch, "E285", {"start": v(10.04, -8.3) * mm, "end": v(9.84, -9.32) * mm});
            skLineSegment(sketch, "E286", {"start": v(9.84, -9.32) * mm, "end": v(9.96, -11) * mm});
            skLineSegment(sketch, "E287", {"start": v(9.96, -11) * mm, "end": v(10.1, -11.4) * mm});
            skLineSegment(sketch, "E288", {"start": v(10.1, -11.4) * mm, "end": v(10.78, -11.76) * mm});
            skLineSegment(sketch, "E289", {"start": v(10.78, -11.76) * mm, "end": v(11.52, -11.99) * mm});
            skLineSegment(sketch, "E290", {"start": v(11.52, -11.99) * mm, "end": v(11.9, -11.8) * mm});
            skLineSegment(sketch, "E291", {"start": v(11.9, -11.8) * mm, "end": v(13.17, -10.7) * mm});
            skLineSegment(sketch, "E292", {"start": v(13.17, -10.7) * mm, "end": v(13.74, -9.84) * mm});
            skLineSegment(sketch, "E293", {"start": v(13.74, -9.84) * mm, "end": v(13.86, -9.5) * mm});
            skLineSegment(sketch, "E294", {"start": v(13.86, -9.5) * mm, "end": v(13.94, -8.32) * mm});
            skLineSegment(sketch, "E295", {"start": v(13.94, -8.32) * mm, "end": v(14.51, -7.59) * mm});
            skLineSegment(sketch, "E296", {"start": v(14.51, -7.59) * mm, "end": v(16.79, -7.59) * mm});
            skLineSegment(sketch, "E297", {"start": v(16.79, -7.59) * mm, "end": v(17.36, -8.32) * mm});
            skLineSegment(sketch, "E298", {"start": v(17.36, -8.32) * mm, "end": v(17.44, -9.5) * mm});
            skLineSegment(sketch, "E299", {"start": v(17.44, -9.5) * mm, "end": v(17.56, -9.84) * mm});
            skLineSegment(sketch, "E300", {"start": v(17.56, -9.84) * mm, "end": v(18.13, -10.7) * mm});
            skLineSegment(sketch, "E301", {"start": v(18.13, -10.7) * mm, "end": v(19.4, -11.8) * mm});
            skLineSegment(sketch, "E302", {"start": v(19.4, -11.8) * mm, "end": v(19.78, -11.99) * mm});
            skLineSegment(sketch, "E303", {"start": v(19.78, -11.99) * mm, "end": v(20.52, -11.76) * mm});
            skLineSegment(sketch, "E304", {"start": v(20.52, -11.76) * mm, "end": v(21.2, -11.4) * mm});
            skLineSegment(sketch, "E305", {"start": v(21.2, -11.4) * mm, "end": v(21.34, -11) * mm});
            skLineSegment(sketch, "E306", {"start": v(21.34, -11) * mm, "end": v(21.46, -9.32) * mm});
            skLineSegment(sketch, "E307", {"start": v(21.46, -9.32) * mm, "end": v(21.26, -8.3) * mm});
            skLineSegment(sketch, "E308", {"start": v(21.26, -8.3) * mm, "end": v(21.1, -7.98) * mm});
            skLineSegment(sketch, "E309", {"start": v(21.1, -7.98) * mm, "end": v(20.32, -7.1) * mm});
            skLineSegment(sketch, "E310", {"start": v(20.32, -7.1) * mm, "end": v(20.21, -6.17) * mm});
            skLineSegment(sketch, "E311", {"start": v(20.21, -6.17) * mm, "end": v(21.82, -4.56) * mm});
            skLineSegment(sketch, "E312", {"start": v(21.82, -4.56) * mm, "end": v(22.74, -4.67) * mm});
            skLineSegment(sketch, "E313", {"start": v(22.74, -4.67) * mm, "end": v(23.63, -5.45) * mm});
            skLineSegment(sketch, "E314", {"start": v(23.63, -5.45) * mm, "end": v(23.96, -5.6) * mm});
            skLineSegment(sketch, "E315", {"start": v(23.96, -5.6) * mm, "end": v(24.97, -5.8) * mm});
            skLineSegment(sketch, "E316", {"start": v(24.97, -5.8) * mm, "end": v(26.66, -5.7) * mm});
            skLineSegment(sketch, "E317", {"start": v(26.66, -5.7) * mm, "end": v(27.05, -5.56) * mm});
            skLineSegment(sketch, "E318", {"start": v(27.05, -5.56) * mm, "end": v(27.41, -4.87) * mm});
            skLineSegment(sketch, "E319", {"start": v(27.41, -4.87) * mm, "end": v(27.64, -4.13) * mm});
            skLineSegment(sketch, "E320", {"start": v(27.64, -4.13) * mm, "end": v(27.46, -3.76) * mm});
            skLineSegment(sketch, "E321", {"start": v(27.46, -3.76) * mm, "end": v(26.35, -2.48) * mm});
            skLineSegment(sketch, "E322", {"start": v(26.35, -2.48) * mm, "end": v(25.5, -1.9) * mm});
            skLineSegment(sketch, "E323", {"start": v(25.5, -1.9) * mm, "end": v(25.15, -1.8) * mm});
            skLineSegment(sketch, "E324", {"start": v(25.15, -1.8) * mm, "end": v(23.97, -1.71) * mm});
            skLineSegment(sketch, "E325", {"start": v(23.97, -1.71) * mm, "end": v(23.24, -1.14) * mm});
            skLineSegment(sketch, "E326", {"start": v(23.24, -1.14) * mm, "end": v(23.24, 1.14) * mm});
            skLineSegment(sketch, "E327", {"start": v(23.24, 1.14) * mm, "end": v(23.97, 1.71) * mm});
            skLineSegment(sketch, "E328", {"start": v(23.97, 1.71) * mm, "end": v(25.15, 1.8) * mm});
            skLineSegment(sketch, "E329", {"start": v(25.15, 1.8) * mm, "end": v(25.5, 1.9) * mm});
            skLineSegment(sketch, "E330", {"start": v(25.5, 1.9) * mm, "end": v(26.35, 2.48) * mm});
            skLineSegment(sketch, "E331", {"start": v(26.35, 2.48) * mm, "end": v(27.46, 3.76) * mm});
            skLineSegment(sketch, "E332", {"start": v(27.46, 3.76) * mm, "end": v(27.64, 4.13) * mm});
            skLineSegment(sketch, "E333", {"start": v(27.64, 4.13) * mm, "end": v(27.41, 4.87) * mm});
            skLineSegment(sketch, "E334", {"start": v(27.41, 4.87) * mm, "end": v(27.05, 5.56) * mm});
            skLineSegment(sketch, "E335", {"start": v(27.05, 5.56) * mm, "end": v(26.66, 5.7) * mm});
            skLineSegment(sketch, "E336", {"start": v(26.66, 5.7) * mm, "end": v(24.97, 5.8) * mm});
            skLineSegment(sketch, "E337", {"start": v(24.97, 5.8) * mm, "end": v(23.96, 5.6) * mm});
            skLineSegment(sketch, "E338", {"start": v(23.96, 5.6) * mm, "end": v(23.63, 5.45) * mm});
            skLineSegment(sketch, "E339", {"start": v(23.63, 5.45) * mm, "end": v(22.74, 4.67) * mm});
            skLineSegment(sketch, "E340", {"start": v(22.74, 4.67) * mm, "end": v(21.82, 4.56) * mm});
            skLineSegment(sketch, "E341", {"start": v(21.82, 4.56) * mm, "end": v(20.21, 6.17) * mm});
            skLineSegment(sketch, "E342", {"start": v(20.21, 6.17) * mm, "end": v(20.32, 7.1) * mm});
            skLineSegment(sketch, "E343", {"start": v(20.32, 7.1) * mm, "end": v(21.1, 7.98) * mm});
            skLineSegment(sketch, "E344", {"start": v(21.1, 7.98) * mm, "end": v(21.26, 8.3) * mm});
            skLineSegment(sketch, "E345", {"start": v(21.26, 8.3) * mm, "end": v(21.46, 9.32) * mm});
            skLineSegment(sketch, "E346", {"start": v(21.46, 9.32) * mm, "end": v(21.34, 11) * mm});
            skLineSegment(sketch, "E347", {"start": v(21.34, 11) * mm, "end": v(21.2, 11.4) * mm});
            skLineSegment(sketch, "E348", {"start": v(21.2, 11.4) * mm, "end": v(20.52, 11.76) * mm});
            skLineSegment(sketch, "E349", {"start": v(20.52, 11.76) * mm, "end": v(19.78, 11.99) * mm});
            skLineSegment(sketch, "E350", {"start": v(19.78, 11.99) * mm, "end": v(19.4, 11.8) * mm});
            skLineSegment(sketch, "E351", {"start": v(19.4, 11.8) * mm, "end": v(18.13, 10.7) * mm});
            skLineSegment(sketch, "E352", {"start": v(18.13, 10.7) * mm, "end": v(17.56, 9.84) * mm});
            skLineSegment(sketch, "E353", {"start": v(17.56, 9.84) * mm, "end": v(17.44, 9.5) * mm});
            skLineSegment(sketch, "E354", {"start": v(17.44, 9.5) * mm, "end": v(17.36, 8.32) * mm});
            skLineSegment(sketch, "E355", {"start": v(17.36, 8.32) * mm, "end": v(16.79, 7.59) * mm});
            skLineSegment(sketch, "E356", {"start": v(16.79, 7.59) * mm, "end": v(14.51, 7.59) * mm});
            skLineSegment(sketch, "E357", {"start": v(14.51, 7.59) * mm, "end": v(13.94, 8.32) * mm});
            skLineSegment(sketch, "E358", {"start": v(13.94, 8.32) * mm, "end": v(13.86, 9.5) * mm});
            skLineSegment(sketch, "E359", {"start": v(13.86, 9.5) * mm, "end": v(13.74, 9.84) * mm});
            skLineSegment(sketch, "E360", {"start": v(13.74, 9.84) * mm, "end": v(13.17, 10.7) * mm});
            skLineSegment(sketch, "E361", {"start": v(13.17, 10.7) * mm, "end": v(11.9, 11.8) * mm});
            skLineSegment(sketch, "E362", {"start": v(11.9, 11.8) * mm, "end": v(11.52, 11.99) * mm});
            skLineSegment(sketch, "E363", {"start": v(11.52, 11.99) * mm, "end": v(10.78, 11.76) * mm});
            skLineSegment(sketch, "E364", {"start": v(10.78, 11.76) * mm, "end": v(10.1, 11.4) * mm});
            skLineSegment(sketch, "E365", {"start": v(10.1, 11.4) * mm, "end": v(9.96, 11) * mm});
            skLineSegment(sketch, "E366", {"start": v(9.96, 11) * mm, "end": v(9.84, 9.32) * mm});
            skLineSegment(sketch, "E367", {"start": v(9.84, 9.32) * mm, "end": v(10.04, 8.3) * mm});
            skLineSegment(sketch, "E368", {"start": v(10.04, 8.3) * mm, "end": v(10.2, 7.98) * mm});
            skLineSegment(sketch, "E369", {"start": v(10.2, 7.98) * mm, "end": v(10.98, 7.1) * mm});
            skLineSegment(sketch, "E370", {"start": v(10.98, 7.1) * mm, "end": v(11.09, 6.17) * mm});
            skLineSegment(sketch, "E371", {"start": v(11.09, 6.17) * mm, "end": v(9.48, 4.56) * mm});
            skLineSegment(sketch, "E372", {"start": v(9.48, 4.56) * mm, "end": v(8.56, 4.67) * mm});
            skLineSegment(sketch, "E373", {"start": v(8.56, 4.67) * mm, "end": v(7.67, 5.45) * mm});
            skLineSegment(sketch, "E374", {"start": v(7.67, 5.45) * mm, "end": v(7.34, 5.6) * mm});
            skLineSegment(sketch, "E375", {"start": v(7.34, 5.6) * mm, "end": v(6.33, 5.8) * mm});
            skLineSegment(sketch, "E376", {"start": v(6.33, 5.8) * mm, "end": v(4.65, 5.7) * mm});
            skLineSegment(sketch, "E377", {"start": v(4.65, 5.7) * mm, "end": v(4.25, 5.56) * mm});
            skLineSegment(sketch, "E378", {"start": v(14.52, 1.65) * mm, "end": v(14.89, 1.85) * mm});
            skLineSegment(sketch, "E379", {"start": v(14.89, 1.85) * mm, "end": v(15.29, 1.97) * mm});
            skLineSegment(sketch, "E380", {"start": v(15.29, 1.97) * mm, "end": v(15.7, 2) * mm});
            skLineSegment(sketch, "E381", {"start": v(15.7, 2) * mm, "end": v(16.12, 1.94) * mm});
            skLineSegment(sketch, "E382", {"start": v(16.12, 1.94) * mm, "end": v(16.51, 1.8) * mm});
            skLineSegment(sketch, "E383", {"start": v(16.51, 1.8) * mm, "end": v(16.87, 1.59) * mm});
            skLineSegment(sketch, "E384", {"start": v(16.87, 1.59) * mm, "end": v(17.17, 1.3) * mm});
            skLineSegment(sketch, "E385", {"start": v(17.17, 1.3) * mm, "end": v(17.4, 0.95) * mm});
            skLineSegment(sketch, "E386", {"start": v(17.4, 0.95) * mm, "end": v(17.57, 0.57) * mm});
            skLineSegment(sketch, "E387", {"start": v(17.57, 0.57) * mm, "end": v(17.64, 0.16) * mm});
            skLineSegment(sketch, "E388", {"start": v(17.64, 0.16) * mm, "end": v(17.63, -0.26) * mm});
            skLineSegment(sketch, "E389", {"start": v(17.63, -0.26) * mm, "end": v(17.54, -0.67) * mm});
            skLineSegment(sketch, "E390", {"start": v(17.54, -0.67) * mm, "end": v(17.36, -1.04) * mm});
            skLineSegment(sketch, "E391", {"start": v(17.36, -1.04) * mm, "end": v(17.1, -1.38) * mm});
            skLineSegment(sketch, "E392", {"start": v(17.1, -1.38) * mm, "end": v(16.78, -1.65) * mm});
            skLineSegment(sketch, "E393", {"start": v(16.78, -1.65) * mm, "end": v(16.42, -1.85) * mm});
            skLineSegment(sketch, "E394", {"start": v(16.42, -1.85) * mm, "end": v(16.01, -1.97) * mm});
            skLineSegment(sketch, "E395", {"start": v(16.01, -1.97) * mm, "end": v(15.6, -2) * mm});
            skLineSegment(sketch, "E396", {"start": v(15.6, -2) * mm, "end": v(15.18, -1.94) * mm});
            skLineSegment(sketch, "E397", {"start": v(15.18, -1.94) * mm, "end": v(14.79, -1.8) * mm});
            skLineSegment(sketch, "E398", {"start": v(14.79, -1.8) * mm, "end": v(14.43, -1.59) * mm});
            skLineSegment(sketch, "E399", {"start": v(14.43, -1.59) * mm, "end": v(14.13, -1.3) * mm});
            skLineSegment(sketch, "E400", {"start": v(14.13, -1.3) * mm, "end": v(13.9, -0.95) * mm});
            skLineSegment(sketch, "E401", {"start": v(13.9, -0.95) * mm, "end": v(13.73, -0.57) * mm});
            skLineSegment(sketch, "E402", {"start": v(13.73, -0.57) * mm, "end": v(13.66, -0.16) * mm});
            skLineSegment(sketch, "E403", {"start": v(13.66, -0.16) * mm, "end": v(13.67, 0.26) * mm});
            skLineSegment(sketch, "E404", {"start": v(13.67, 0.26) * mm, "end": v(13.77, 0.67) * mm});
            skLineSegment(sketch, "E405", {"start": v(13.77, 0.67) * mm, "end": v(13.95, 1.04) * mm});
            skLineSegment(sketch, "E406", {"start": v(13.95, 1.04) * mm, "end": v(14.2, 1.38) * mm});
            skLineSegment(sketch, "E407", {"start": v(14.2, 1.38) * mm, "end": v(14.52, 1.65) * mm});
            skSolve(sketch);
        }
        {
            var Q0;
            Q0 = qSketchRegion(id + "F0", true);
            extrude(context, id + "F1", {"entities" : qUnion([Q0]), "depth" : 4 * mm, "offsetDistance" : 25 * mm});
        }
        {
            var Q0;
            Q0=makeQuery(id+"F1.opExtrude","CAP_FACE",FACE,{"disambiguationData":[OSD([sQuery(id+"F0.wireOp",EDGE,"E258"),sQuery(id+"F0.wireOp",EDGE,"E259"),sQuery(id+"F0.wireOp",EDGE,"E260"),sQuery(id+"F0.wireOp",EDGE,"E261"),sQuery(id+"F0.wireOp",EDGE,"E262"),sQuery(id+"F0.wireOp",EDGE,"E263"),sQuery(id+"F0.wireOp",EDGE,"E264"),sQuery(id+"F0.wireOp",EDGE,"E265"),sQuery(id+"F0.wireOp",EDGE,"E266"),sQuery(id+"F0.wireOp",EDGE,"E267"),sQuery(id+"F0.wireOp",EDGE,"E268"),sQuery(id+"F0.wireOp",EDGE,"E269"),sQuery(id+"F0.wireOp",EDGE,"E270"),sQuery(id+"F0.wireOp",EDGE,"E271"),sQuery(id+"F0.wireOp",EDGE,"E272"),sQuery(id+"F0.wireOp",EDGE,"E273"),sQuery(id+"F0.wireOp",EDGE,"E274"),sQuery(id+"F0.wireOp",EDGE,"E275"),sQuery(id+"F0.wireOp",EDGE,"E276"),sQuery(id+"F0.wireOp",EDGE,"E277"),sQuery(id+"F0.wireOp",EDGE,"E278"),sQuery(id+"F0.wireOp",EDGE,"E279"),sQuery(id+"F0.wireOp",EDGE,"E280"),sQuery(id+"F0.wireOp",EDGE,"E281"),sQuery(id+"F0.wireOp",EDGE,"E282"),sQuery(id+"F0.wireOp",EDGE,"E283"),sQuery(id+"F0.wireOp",EDGE,"E284"),sQuery(id+"F0.wireOp",EDGE,"E285"),sQuery(id+"F0.wireOp",EDGE,"E286"),sQuery(id+"F0.wireOp",EDGE,"E287"),sQuery(id+"F0.wireOp",EDGE,"E288"),sQuery(id+"F0.wireOp",EDGE,"E289"),sQuery(id+"F0.wireOp",EDGE,"E290"),sQuery(id+"F0.wireOp",EDGE,"E291"),sQuery(id+"F0.wireOp",EDGE,"E292"),sQuery(id+"F0.wireOp",EDGE,"E293"),sQuery(id+"F0.wireOp",EDGE,"E294"),sQuery(id+"F0.wireOp",EDGE,"E295"),sQuery(id+"F0.wireOp",EDGE,"E296"),sQuery(id+"F0.wireOp",EDGE,"E297"),sQuery(id+"F0.wireOp",EDGE,"E298"),sQuery(id+"F0.wireOp",EDGE,"E299"),sQuery(id+"F0.wireOp",EDGE,"E300"),sQuery(id+"F0.wireOp",EDGE,"E301"),sQuery(id+"F0.wireOp",EDGE,"E302"),sQuery(id+"F0.wireOp",EDGE,"E303"),sQuery(id+"F0.wireOp",EDGE,"E304"),sQuery(id+"F0.wireOp",EDGE,"E305"),sQuery(id+"F0.wireOp",EDGE,"E306"),sQuery(id+"F0.wireOp",EDGE,"E307"),sQuery(id+"F0.wireOp",EDGE,"E308"),sQuery(id+"F0.wireOp",EDGE,"E309"),sQuery(id+"F0.wireOp",EDGE,"E310"),sQuery(id+"F0.wireOp",EDGE,"E311"),sQuery(id+"F0.wireOp",EDGE,"E312"),sQuery(id+"F0.wireOp",EDGE,"E313"),sQuery(id+"F0.wireOp",EDGE,"E314"),sQuery(id+"F0.wireOp",EDGE,"E315"),sQuery(id+"F0.wireOp",EDGE,"E316"),sQuery(id+"F0.wireOp",EDGE,"E317"),sQuery(id+"F0.wireOp",EDGE,"E318"),sQuery(id+"F0.wireOp",EDGE,"E319"),sQuery(id+"F0.wireOp",EDGE,"E320"),sQuery(id+"F0.wireOp",EDGE,"E321"),sQuery(id+"F0.wireOp",EDGE,"E322"),sQuery(id+"F0.wireOp",EDGE,"E323"),sQuery(id+"F0.wireOp",EDGE,"E324"),sQuery(id+"F0.wireOp",EDGE,"E325"),sQuery(id+"F0.wireOp",EDGE,"E326"),sQuery(id+"F0.wireOp",EDGE,"E327"),sQuery(id+"F0.wireOp",EDGE,"E328"),sQuery(id+"F0.wireOp",EDGE,"E329"),sQuery(id+"F0.wireOp",EDGE,"E330"),sQuery(id+"F0.wireOp",EDGE,"E331"),sQuery(id+"F0.wireOp",EDGE,"E332"),sQuery(id+"F0.wireOp",EDGE,"E333"),sQuery(id+"F0.wireOp",EDGE,"E334"),sQuery(id+"F0.wireOp",EDGE,"E335"),sQuery(id+"F0.wireOp",EDGE,"E336"),sQuery(id+"F0.wireOp",EDGE,"E337"),sQuery(id+"F0.wireOp",EDGE,"E338"),sQuery(id+"F0.wireOp",EDGE,"E339"),sQuery(id+"F0.wireOp",EDGE,"E340"),sQuery(id+"F0.wireOp",EDGE,"E341"),sQuery(id+"F0.wireOp",EDGE,"E342"),sQuery(id+"F0.wireOp",EDGE,"E343"),sQuery(id+"F0.wireOp",EDGE,"E344"),sQuery(id+"F0.wireOp",EDGE,"E345"),sQuery(id+"F0.wireOp",EDGE,"E346"),sQuery(id+"F0.wireOp",EDGE,"E347"),sQuery(id+"F0.wireOp",EDGE,"E348"),sQuery(id+"F0.wireOp",EDGE,"E349"),sQuery(id+"F0.wireOp",EDGE,"E350"),sQuery(id+"F0.wireOp",EDGE,"E351"),sQuery(id+"F0.wireOp",EDGE,"E352"),sQuery(id+"F0.wireOp",EDGE,"E353"),sQuery(id+"F0.wireOp",EDGE,"E354"),sQuery(id+"F0.wireOp",EDGE,"E355"),sQuery(id+"F0.wireOp",EDGE,"E356"),sQuery(id+"F0.wireOp",EDGE,"E357"),sQuery(id+"F0.wireOp",EDGE,"E358"),sQuery(id+"F0.wireOp",EDGE,"E359"),sQuery(id+"F0.wireOp",EDGE,"E360"),sQuery(id+"F0.wireOp",EDGE,"E361"),sQuery(id+"F0.wireOp",EDGE,"E362"),sQuery(id+"F0.wireOp",EDGE,"E363"),sQuery(id+"F0.wireOp",EDGE,"E364"),sQuery(id+"F0.wireOp",EDGE,"E365"),sQuery(id+"F0.wireOp",EDGE,"E366"),sQuery(id+"F0.wireOp",EDGE,"E367"),sQuery(id+"F0.wireOp",EDGE,"E368"),sQuery(id+"F0.wireOp",EDGE,"E369"),sQuery(id+"F0.wireOp",EDGE,"E370"),sQuery(id+"F0.wireOp",EDGE,"E371"),sQuery(id+"F0.wireOp",EDGE,"E372"),sQuery(id+"F0.wireOp",EDGE,"E373"),sQuery(id+"F0.wireOp",EDGE,"E374"),sQuery(id+"F0.wireOp",EDGE,"E375"),sQuery(id+"F0.wireOp",EDGE,"E376"),sQuery(id+"F0.wireOp",EDGE,"E377"),sQuery(id+"F0.wireOp",EDGE,"E378"),sQuery(id+"F0.wireOp",EDGE,"E379"),sQuery(id+"F0.wireOp",EDGE,"E380"),sQuery(id+"F0.wireOp",EDGE,"E381"),sQuery(id+"F0.wireOp",EDGE,"E382"),sQuery(id+"F0.wireOp",EDGE,"E383"),sQuery(id+"F0.wireOp",EDGE,"E384"),sQuery(id+"F0.wireOp",EDGE,"E385"),sQuery(id+"F0.wireOp",EDGE,"E386"),sQuery(id+"F0.wireOp",EDGE,"E387"),sQuery(id+"F0.wireOp",EDGE,"E388"),sQuery(id+"F0.wireOp",EDGE,"E389"),sQuery(id+"F0.wireOp",EDGE,"E390"),sQuery(id+"F0.wireOp",EDGE,"E391"),sQuery(id+"F0.wireOp",EDGE,"E392"),sQuery(id+"F0.wireOp",EDGE,"E393"),sQuery(id+"F0.wireOp",EDGE,"E394"),sQuery(id+"F0.wireOp",EDGE,"E395"),sQuery(id+"F0.wireOp",EDGE,"E396"),sQuery(id+"F0.wireOp",EDGE,"E397"),sQuery(id+"F0.wireOp",EDGE,"E398"),sQuery(id+"F0.wireOp",EDGE,"E399"),sQuery(id+"F0.wireOp",EDGE,"E400"),sQuery(id+"F0.wireOp",EDGE,"E401"),sQuery(id+"F0.wireOp",EDGE,"E402"),sQuery(id+"F0.wireOp",EDGE,"E403"),sQuery(id+"F0.wireOp",EDGE,"E404"),sQuery(id+"F0.wireOp",EDGE,"E405"),sQuery(id+"F0.wireOp",EDGE,"E406"),sQuery(id+"F0.wireOp",EDGE,"E407")])],"isStart":false});
            var sketch = newSketch(context, id + "F2", { "sketchPlane" : qUnion([Q0])});
            skCircle(sketch, "E408", {"center": v(15.65, 0) * mm, "radius": 2.5 * mm});
            skLineSegment(sketch, "E409", {"start": v(14.01, -1.13) * mm, "end": v(16.12, 0.32) * mm, "construction": true});
            skLineSegment(sketch, "E410", {"start": v(15.09, 1.9) * mm, "end": v(15.86, -0.71) * mm, "construction": true});
            skSolve(sketch);
        }
        {
            var Q0;
            Q0 = qSketchRegion(id + "F2", true);
            extrude(context, id + "F3", {"entities" : qUnion([Q0]), "operationType" : NewBodyOperationType.REMOVE, "oppositeDirection" : true, "depth" : 25 * mm, "offsetDistance" : 25 * mm});
        }
        {
            var Q0;
            Q0=makeQuery(id+"F1.opExtrude","CAP_FACE",FACE,{"disambiguationData":[OSD([sQuery(id+"F0.wireOp",EDGE,"E0"),sQuery(id+"F0.wireOp",EDGE,"E1"),sQuery(id+"F0.wireOp",EDGE,"E2"),sQuery(id+"F0.wireOp",EDGE,"E3"),sQuery(id+"F0.wireOp",EDGE,"E4"),sQuery(id+"F0.wireOp",EDGE,"E5"),sQuery(id+"F0.wireOp",EDGE,"E6"),sQuery(id+"F0.wireOp",EDGE,"E7"),sQuery(id+"F0.wireOp",EDGE,"E8"),sQuery(id+"F0.wireOp",EDGE,"E9"),sQuery(id+"F0.wireOp",EDGE,"E10"),sQuery(id+"F0.wireOp",EDGE,"E11"),sQuery(id+"F0.wireOp",EDGE,"E12"),sQuery(id+"F0.wireOp",EDGE,"E13"),sQuery(id+"F0.wireOp",EDGE,"E14"),sQuery(id+"F0.wireOp",EDGE,"E15"),sQuery(id+"F0.wireOp",EDGE,"E16"),sQuery(id+"F0.wireOp",EDGE,"E17"),sQuery(id+"F0.wireOp",EDGE,"E18"),sQuery(id+"F0.wireOp",EDGE,"E19"),sQuery(id+"F0.wireOp",EDGE,"E20"),sQuery(id+"F0.wireOp",EDGE,"E21"),sQuery(id+"F0.wireOp",EDGE,"E22"),sQuery(id+"F0.wireOp",EDGE,"E23"),sQuery(id+"F0.wireOp",EDGE,"E24"),sQuery(id+"F0.wireOp",EDGE,"E25"),sQuery(id+"F0.wireOp",EDGE,"E26"),sQuery(id+"F0.wireOp",EDGE,"E27"),sQuery(id+"F0.wireOp",EDGE,"E28"),sQuery(id+"F0.wireOp",EDGE,"E29"),sQuery(id+"F0.wireOp",EDGE,"E30"),sQuery(id+"F0.wireOp",EDGE,"E31"),sQuery(id+"F0.wireOp",EDGE,"E32"),sQuery(id+"F0.wireOp",EDGE,"E33"),sQuery(id+"F0.wireOp",EDGE,"E34"),sQuery(id+"F0.wireOp",EDGE,"E35"),sQuery(id+"F0.wireOp",EDGE,"E36"),sQuery(id+"F0.wireOp",EDGE,"E37"),sQuery(id+"F0.wireOp",EDGE,"E38"),sQuery(id+"F0.wireOp",EDGE,"E39"),sQuery(id+"F0.wireOp",EDGE,"E40"),sQuery(id+"F0.wireOp",EDGE,"E41"),sQuery(id+"F0.wireOp",EDGE,"E42"),sQuery(id+"F0.wireOp",EDGE,"E43"),sQuery(id+"F0.wireOp",EDGE,"E44"),sQuery(id+"F0.wireOp",EDGE,"E45"),sQuery(id+"F0.wireOp",EDGE,"E46"),sQuery(id+"F0.wireOp",EDGE,"E47"),sQuery(id+"F0.wireOp",EDGE,"E48"),sQuery(id+"F0.wireOp",EDGE,"E49"),sQuery(id+"F0.wireOp",EDGE,"E50"),sQuery(id+"F0.wireOp",EDGE,"E51"),sQuery(id+"F0.wireOp",EDGE,"E52"),sQuery(id+"F0.wireOp",EDGE,"E53"),sQuery(id+"F0.wireOp",EDGE,"E54"),sQuery(id+"F0.wireOp",EDGE,"E55"),sQuery(id+"F0.wireOp",EDGE,"E56"),sQuery(id+"F0.wireOp",EDGE,"E57"),sQuery(id+"F0.wireOp",EDGE,"E58"),sQuery(id+"F0.wireOp",EDGE,"E59"),sQuery(id+"F0.wireOp",EDGE,"E60"),sQuery(id+"F0.wireOp",EDGE,"E61"),sQuery(id+"F0.wireOp",EDGE,"E62"),sQuery(id+"F0.wireOp",EDGE,"E63"),sQuery(id+"F0.wireOp",EDGE,"E64"),sQuery(id+"F0.wireOp",EDGE,"E65"),sQuery(id+"F0.wireOp",EDGE,"E66"),sQuery(id+"F0.wireOp",EDGE,"E67"),sQuery(id+"F0.wireOp",EDGE,"E68"),sQuery(id+"F0.wireOp",EDGE,"E69"),sQuery(id+"F0.wireOp",EDGE,"E70"),sQuery(id+"F0.wireOp",EDGE,"E71"),sQuery(id+"F0.wireOp",EDGE,"E72"),sQuery(id+"F0.wireOp",EDGE,"E73"),sQuery(id+"F0.wireOp",EDGE,"E74"),sQuery(id+"F0.wireOp",EDGE,"E75"),sQuery(id+"F0.wireOp",EDGE,"E76"),sQuery(id+"F0.wireOp",EDGE,"E77"),sQuery(id+"F0.wireOp",EDGE,"E78"),sQuery(id+"F0.wireOp",EDGE,"E79"),sQuery(id+"F0.wireOp",EDGE,"E80"),sQuery(id+"F0.wireOp",EDGE,"E81"),sQuery(id+"F0.wireOp",EDGE,"E82"),sQuery(id+"F0.wireOp",EDGE,"E83"),sQuery(id+"F0.wireOp",EDGE,"E84"),sQuery(id+"F0.wireOp",EDGE,"E85"),sQuery(id+"F0.wireOp",EDGE,"E86"),sQuery(id+"F0.wireOp",EDGE,"E87"),sQuery(id+"F0.wireOp",EDGE,"E88"),sQuery(id+"F0.wireOp",EDGE,"E89"),sQuery(id+"F0.wireOp",EDGE,"E90"),sQuery(id+"F0.wireOp",EDGE,"E91"),sQuery(id+"F0.wireOp",EDGE,"E92"),sQuery(id+"F0.wireOp",EDGE,"E93"),sQuery(id+"F0.wireOp",EDGE,"E94"),sQuery(id+"F0.wireOp",EDGE,"E95"),sQuery(id+"F0.wireOp",EDGE,"E96"),sQuery(id+"F0.wireOp",EDGE,"E97"),sQuery(id+"F0.wireOp",EDGE,"E98"),sQuery(id+"F0.wireOp",EDGE,"E99"),sQuery(id+"F0.wireOp",EDGE,"E100"),sQuery(id+"F0.wireOp",EDGE,"E101"),sQuery(id+"F0.wireOp",EDGE,"E102"),sQuery(id+"F0.wireOp",EDGE,"E103"),sQuery(id+"F0.wireOp",EDGE,"E104"),sQuery(id+"F0.wireOp",EDGE,"E105"),sQuery(id+"F0.wireOp",EDGE,"E106"),sQuery(id+"F0.wireOp",EDGE,"E107"),sQuery(id+"F0.wireOp",EDGE,"E108"),sQuery(id+"F0.wireOp",EDGE,"E109"),sQuery(id+"F0.wireOp",EDGE,"E110"),sQuery(id+"F0.wireOp",EDGE,"E111"),sQuery(id+"F0.wireOp",EDGE,"E112"),sQuery(id+"F0.wireOp",EDGE,"E113"),sQuery(id+"F0.wireOp",EDGE,"E114"),sQuery(id+"F0.wireOp",EDGE,"E115"),sQuery(id+"F0.wireOp",EDGE,"E116"),sQuery(id+"F0.wireOp",EDGE,"E117"),sQuery(id+"F0.wireOp",EDGE,"E118"),sQuery(id+"F0.wireOp",EDGE,"E119"),sQuery(id+"F0.wireOp",EDGE,"E120"),sQuery(id+"F0.wireOp",EDGE,"E121"),sQuery(id+"F0.wireOp",EDGE,"E122"),sQuery(id+"F0.wireOp",EDGE,"E123"),sQuery(id+"F0.wireOp",EDGE,"E124"),sQuery(id+"F0.wireOp",EDGE,"E125"),sQuery(id+"F0.wireOp",EDGE,"E126"),sQuery(id+"F0.wireOp",EDGE,"E127"),sQuery(id+"F0.wireOp",EDGE,"E128"),sQuery(id+"F0.wireOp",EDGE,"E129"),sQuery(id+"F0.wireOp",EDGE,"E130"),sQuery(id+"F0.wireOp",EDGE,"E131"),sQuery(id+"F0.wireOp",EDGE,"E132"),sQuery(id+"F0.wireOp",EDGE,"E133"),sQuery(id+"F0.wireOp",EDGE,"E134"),sQuery(id+"F0.wireOp",EDGE,"E135"),sQuery(id+"F0.wireOp",EDGE,"E136"),sQuery(id+"F0.wireOp",EDGE,"E137"),sQuery(id+"F0.wireOp",EDGE,"E138"),sQuery(id+"F0.wireOp",EDGE,"E139"),sQuery(id+"F0.wireOp",EDGE,"E140"),sQuery(id+"F0.wireOp",EDGE,"E141"),sQuery(id+"F0.wireOp",EDGE,"E142"),sQuery(id+"F0.wireOp",EDGE,"E143"),sQuery(id+"F0.wireOp",EDGE,"E144"),sQuery(id+"F0.wireOp",EDGE,"E145"),sQuery(id+"F0.wireOp",EDGE,"E146"),sQuery(id+"F0.wireOp",EDGE,"E147"),sQuery(id+"F0.wireOp",EDGE,"E148"),sQuery(id+"F0.wireOp",EDGE,"E149"),sQuery(id+"F0.wireOp",EDGE,"E150"),sQuery(id+"F0.wireOp",EDGE,"E151"),sQuery(id+"F0.wireOp",EDGE,"E152"),sQuery(id+"F0.wireOp",EDGE,"E153"),sQuery(id+"F0.wireOp",EDGE,"E154"),sQuery(id+"F0.wireOp",EDGE,"E155"),sQuery(id+"F0.wireOp",EDGE,"E156"),sQuery(id+"F0.wireOp",EDGE,"E157"),sQuery(id+"F0.wireOp",EDGE,"E158"),sQuery(id+"F0.wireOp",EDGE,"E159"),sQuery(id+"F0.wireOp",EDGE,"E160"),sQuery(id+"F0.wireOp",EDGE,"E161"),sQuery(id+"F0.wireOp",EDGE,"E162"),sQuery(id+"F0.wireOp",EDGE,"E163"),sQuery(id+"F0.wireOp",EDGE,"E164"),sQuery(id+"F0.wireOp",EDGE,"E165"),sQuery(id+"F0.wireOp",EDGE,"E166"),sQuery(id+"F0.wireOp",EDGE,"E167"),sQuery(id+"F0.wireOp",EDGE,"E168"),sQuery(id+"F0.wireOp",EDGE,"E169"),sQuery(id+"F0.wireOp",EDGE,"E170"),sQuery(id+"F0.wireOp",EDGE,"E171"),sQuery(id+"F0.wireOp",EDGE,"E172"),sQuery(id+"F0.wireOp",EDGE,"E173"),sQuery(id+"F0.wireOp",EDGE,"E174"),sQuery(id+"F0.wireOp",EDGE,"E175"),sQuery(id+"F0.wireOp",EDGE,"E176"),sQuery(id+"F0.wireOp",EDGE,"E177"),sQuery(id+"F0.wireOp",EDGE,"E178"),sQuery(id+"F0.wireOp",EDGE,"E179"),sQuery(id+"F0.wireOp",EDGE,"E180"),sQuery(id+"F0.wireOp",EDGE,"E181"),sQuery(id+"F0.wireOp",EDGE,"E182"),sQuery(id+"F0.wireOp",EDGE,"E183"),sQuery(id+"F0.wireOp",EDGE,"E184"),sQuery(id+"F0.wireOp",EDGE,"E185"),sQuery(id+"F0.wireOp",EDGE,"E186"),sQuery(id+"F0.wireOp",EDGE,"E187"),sQuery(id+"F0.wireOp",EDGE,"E188"),sQuery(id+"F0.wireOp",EDGE,"E189"),sQuery(id+"F0.wireOp",EDGE,"E190"),sQuery(id+"F0.wireOp",EDGE,"E191"),sQuery(id+"F0.wireOp",EDGE,"E192"),sQuery(id+"F0.wireOp",EDGE,"E193"),sQuery(id+"F0.wireOp",EDGE,"E194"),sQuery(id+"F0.wireOp",EDGE,"E195"),sQuery(id+"F0.wireOp",EDGE,"E196"),sQuery(id+"F0.wireOp",EDGE,"E197"),sQuery(id+"F0.wireOp",EDGE,"E198"),sQuery(id+"F0.wireOp",EDGE,"E199"),sQuery(id+"F0.wireOp",EDGE,"E200"),sQuery(id+"F0.wireOp",EDGE,"E201"),sQuery(id+"F0.wireOp",EDGE,"E202"),sQuery(id+"F0.wireOp",EDGE,"E203"),sQuery(id+"F0.wireOp",EDGE,"E204"),sQuery(id+"F0.wireOp",EDGE,"E205"),sQuery(id+"F0.wireOp",EDGE,"E206"),sQuery(id+"F0.wireOp",EDGE,"E207"),sQuery(id+"F0.wireOp",EDGE,"E208"),sQuery(id+"F0.wireOp",EDGE,"E209"),sQuery(id+"F0.wireOp",EDGE,"E210"),sQuery(id+"F0.wireOp",EDGE,"E211"),sQuery(id+"F0.wireOp",EDGE,"E212"),sQuery(id+"F0.wireOp",EDGE,"E213"),sQuery(id+"F0.wireOp",EDGE,"E214"),sQuery(id+"F0.wireOp",EDGE,"E215"),sQuery(id+"F0.wireOp",EDGE,"E216"),sQuery(id+"F0.wireOp",EDGE,"E217"),sQuery(id+"F0.wireOp",EDGE,"E218"),sQuery(id+"F0.wireOp",EDGE,"E219"),sQuery(id+"F0.wireOp",EDGE,"E220"),sQuery(id+"F0.wireOp",EDGE,"E221"),sQuery(id+"F0.wireOp",EDGE,"E222"),sQuery(id+"F0.wireOp",EDGE,"E223"),sQuery(id+"F0.wireOp",EDGE,"E224"),sQuery(id+"F0.wireOp",EDGE,"E225"),sQuery(id+"F0.wireOp",EDGE,"E226"),sQuery(id+"F0.wireOp",EDGE,"E227"),sQuery(id+"F0.wireOp",EDGE,"E228"),sQuery(id+"F0.wireOp",EDGE,"E229"),sQuery(id+"F0.wireOp",EDGE,"E230"),sQuery(id+"F0.wireOp",EDGE,"E231"),sQuery(id+"F0.wireOp",EDGE,"E232"),sQuery(id+"F0.wireOp",EDGE,"E233"),sQuery(id+"F0.wireOp",EDGE,"E234"),sQuery(id+"F0.wireOp",EDGE,"E235"),sQuery(id+"F0.wireOp",EDGE,"E236"),sQuery(id+"F0.wireOp",EDGE,"E237"),sQuery(id+"F0.wireOp",EDGE,"E238"),sQuery(id+"F0.wireOp",EDGE,"E239"),sQuery(id+"F0.wireOp",EDGE,"E240"),sQuery(id+"F0.wireOp",EDGE,"E241"),sQuery(id+"F0.wireOp",EDGE,"E242"),sQuery(id+"F0.wireOp",EDGE,"E243"),sQuery(id+"F0.wireOp",EDGE,"E244"),sQuery(id+"F0.wireOp",EDGE,"E245"),sQuery(id+"F0.wireOp",EDGE,"E246"),sQuery(id+"F0.wireOp",EDGE,"E247"),sQuery(id+"F0.wireOp",EDGE,"E248"),sQuery(id+"F0.wireOp",EDGE,"E249"),sQuery(id+"F0.wireOp",EDGE,"E250"),sQuery(id+"F0.wireOp",EDGE,"E251"),sQuery(id+"F0.wireOp",EDGE,"E252"),sQuery(id+"F0.wireOp",EDGE,"E253"),sQuery(id+"F0.wireOp",EDGE,"E254"),sQuery(id+"F0.wireOp",EDGE,"E255"),sQuery(id+"F0.wireOp",EDGE,"E256"),sQuery(id+"F0.wireOp",EDGE,"E257")])],"isStart":false});
            var sketch = newSketch(context, id + "F4", { "sketchPlane" : qUnion([Q0])});
            skLineSegment(sketch, "E411", {"start": v(-8.2, -1.17) * mm, "end": v(-10.25, 0.32) * mm, "construction": true});
            skLineSegment(sketch, "E412", {"start": v(-8.48, 1.48) * mm, "end": v(-10.15, -0.37) * mm, "construction": true});
            skCircle(sketch, "E413", {"center": v(-9.81, 0) * mm, "radius": 3.25 * mm});
            skSolve(sketch);
        }
        {
            var Q0;
            Q0 = qSketchRegion(id + "F4", true);
            extrude(context, id + "F5", {"entities" : qUnion([Q0]), "operationType" : NewBodyOperationType.REMOVE, "oppositeDirection" : true, "depth" : 25 * mm, "offsetDistance" : 25 * mm});
        }
    });
